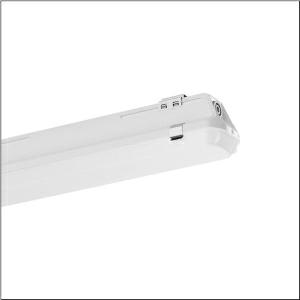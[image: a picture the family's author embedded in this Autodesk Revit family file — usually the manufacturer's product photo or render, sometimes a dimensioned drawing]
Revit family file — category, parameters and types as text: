
# Revit family: monsun_r__11_parking_51fg20dp440h_7f6a
name_source: partatom
category: Lighting Fixtures
units: mm (PartAtom-declared; Revit-internal decimal feet)

## family parameters
Cut with Voids When Loaded = No
Host = Face
Light Source = No
Part Type = Normal
Room Calculation Point = No
Round Connector Dimension = Use Diameter
Shared = No

## types (1)
- --- (1 x LED, 4840 lm, 30.8 W, 4000K)
    Apparent Load = 31 VA
    CIE Flux Codes = 45 75 93 94 100
    Color Rendering = 80
    Color Temperature = 4000K
    Default Elevation = 1800 mm
    Description = Monsun® 11 parking, damp-proof luminaire, chain hanger, primary optical cover: enclosure, of PC, light emission: direct distribution, primary light characteristic: symmetric, installation type: suspended mounting, surface-mounted, horizontal mounting, vertical mounting, LED, rated luminous flux: 4.840lm, luminous efficacy: 157lm/W, light colour: 840, colour temperature: 4000K, control gear: ECG DALI, with terminal, 5-pole, max. 2.5mm², mains connection: 220..240V, AC, 50/60Hz, rated input power: 31W, housing, of glass-fibre reinforced polyester, uncoated, bright grey, incl. chain hanger, length: 1.590mm, width: 90mm, height: 88mm, clip for enclosure, of stainless steel (V2A), ceiling mounting element, of stainless steel (V2A), chain hanger, of stainless steel (V2A), protection rating (complete): IP66, insulation class (complete): insulation class I (protective earthing), certification: CE, ENEC, VDE, UKCA, protection symbol: D, impact resistance: IK08, permissible operating ambient temperature: -25..+40°C, standard: EN 50419, EN 60598-2-1, no direct snow, no direct sun, no direct rain, for indoor or canopied outdoor use, corresponds to IFS (International Featured Standards) requirements for safety and quality in the food industry, contact your sales advisor before using the luminaires in applications with unclear chemical exposure, large temperature fluctuations or condensation-forming humidity, LABS conformity tested according to VDMA 24364:2018-05, packaging unit: 1 piece
    Height = 89 mm
    Lamp = 1 x LED
    Lamp Light Flux = 4840 lm
    Lamp Power = 30.8 W
    Lamp count = 1
    Length = 1590 mm
    Luminous efficacy = 157 lm/W
    Manufacturer = Siteco
    ModVariant = No
    Model = 51FG20DP440H
    Mounting Place = Ceiling
    Mounting Type = Surface mounted
    Number of Poles = 1
    OnlyDefault = Yes
    Power Factor = 1
    Product Name = Monsun® 11 parking
    Product group = damp-proof luminaire
    ProductGroupID = 301
    Protection Class = Protection class I
    Protection Degree = IP 66
    RLX_Detail_Level = 1
    RLX_Emergency_Light_Flux = 0 lm
    RLX_Emergency_Type = 0
    RLX_Emergency_Type_DB = No
    RlxData = <blob elided: 92045 chars, md5=2f80a8d6>
    Socket = socket
    Standby Power = 0 W
    System Light Flux = 4840 lm
    System Power = 31 W
    Type Comments = factory setting: luminous flux: 100 % | dim-lin: 254 | 205 mA
    Type Image = l_1004748.jpg
    URL = http://relux.com
    VarID = @adj_156305
    Voltage = 0 V
    Weight = 0.00 kg
    Width = 90 mm

## geometry (parser evidence)
native form markers: Blend x4, Sweep x13
no freeform markers — native parametric forms only
